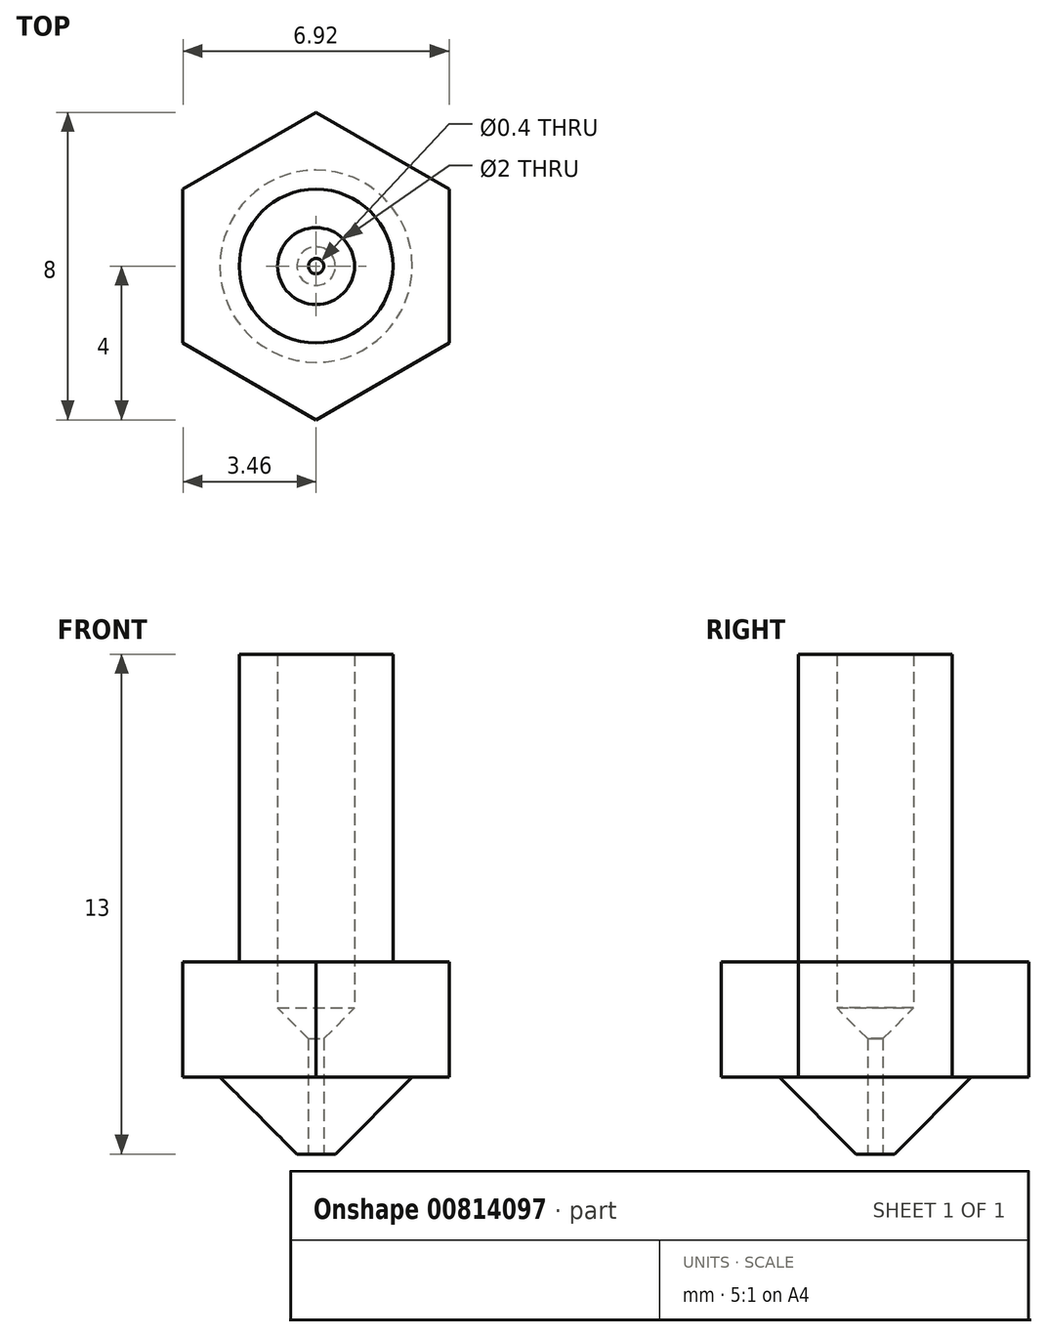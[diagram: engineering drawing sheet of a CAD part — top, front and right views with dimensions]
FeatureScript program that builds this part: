
annotation { "Feature Type Name" : "Feature", "Feature Type Description" : "" }
export const myFeature = defineFeature(function(context is Context, id is Id, definition is map)
    precondition{}
    {
        {
            var Q0;
            Q0=qCreatedBy(makeId("Front.planeOp"),FACE);
            var sketch = newSketch(context, id + "F0", { "sketchPlane" : qUnion([Q0])});
            skLineSegment(sketch, "E0", {"start": v(0, 0) * mm, "end": v(0, 10.14) * mm, "construction": true});
            skLineSegment(sketch, "E1", {"start": v(0.2, 0) * mm, "end": v(0.5, 0) * mm});
            skLineSegment(sketch, "E2", {"start": v(0.5, 0) * mm, "end": v(2.5, 2) * mm});
            skLineSegment(sketch, "E3", {"start": v(2.5, 2) * mm, "end": v(4, 2) * mm});
            skLineSegment(sketch, "E4", {"start": v(4, 2) * mm, "end": v(4, 5) * mm});
            skLineSegment(sketch, "E5", {"start": v(4, 5) * mm, "end": v(2, 5) * mm});
            skLineSegment(sketch, "E6", {"start": v(2, 5) * mm, "end": v(2, 13) * mm});
            skLineSegment(sketch, "E7", {"start": v(2, 13) * mm, "end": v(0.2, 13) * mm});
            skLineSegment(sketch, "E8", {"start": v(0.2, 13) * mm, "end": v(0.2, 0) * mm});
            skLineSegment(sketch, "E9", {"start": v(1, 13) * mm, "end": v(1, 3.8) * mm});
            skLineSegment(sketch, "E10", {"start": v(1, 3.8) * mm, "end": v(0.2, 3) * mm});
            skSolve(sketch);
        }
        {
            var Q0;
            {var subQ0=sQuery(id+"F0.wireOp",EDGE,"E1");Q0=makeQuery(id+"F0.imprint","IMPRINT",FACE,{"disambiguationData":[TD([[makeQuery(id+"F0.imprint","IMPRINT",EDGE,{"derivedFrom":subQ0}),1.0]])]});}
            var Q1;
            Q1=sQuery(id+"F0.wireOp",EDGE,"E0");
            revolve(context, id + "F1", {"surfaceOperationType" : NewSurfaceOperationType.NEW, "entities" : qUnion([Q0]), "axis" : qUnion([Q1]), "revolveType" : RevolveType.FULL});
        }
        {
            var Q0;
            Q0=makeQuery(id+"F1.opRevolve","SWEPT_FACE",FACE,{"disambiguationData":[OSD([sQuery(id+"F0.wireOp",EDGE,"E3")])]});
            var sketch = newSketch(context, id + "F2", { "sketchPlane" : qUnion([Q0])});
            skCircle(sketch, "E11.cCircle", {"center": v(0, 0) * mm, "radius": 3.46 * mm, "construction": true});
            skLineSegment(sketch, "E11.0", {"start": v(3.46, 2) * mm, "end": v(3.46, -2) * mm});
            skLineSegment(sketch, "E11.1", {"start": v(3.46, -2) * mm, "end": v(0, -4) * mm});
            skLineSegment(sketch, "E11.2", {"start": v(0, -4) * mm, "end": v(-3.46, -2) * mm});
            skLineSegment(sketch, "E11.3", {"start": v(-3.46, -2) * mm, "end": v(-3.46, 2) * mm});
            skLineSegment(sketch, "E11.4", {"start": v(-3.46, 2) * mm, "end": v(0, 4) * mm});
            skLineSegment(sketch, "E11.5", {"start": v(0, 4) * mm, "end": v(3.46, 2) * mm});
            skPoint(sketch, "E11.0.midPoint", {"position": v(3.46, 0) * mm});
            skSolve(sketch);
        }
        {
            var Q0;
            {var subQ0=sQuery(id+"F2.wireOp",EDGE,"E11.4");Q0=makeQuery(id+"F2.imprint","IMPRINT",FACE,{"disambiguationData":[TD([[makeQuery(id+"F2.imprint","IMPRINT",EDGE,{"derivedFrom":subQ0}),1.0]])]});}
            var Q1;
            {var subQ0=sQuery(id+"F2.wireOp",EDGE,"E11.5");Q1=makeQuery(id+"F2.imprint","IMPRINT",FACE,{"disambiguationData":[TD([[makeQuery(id+"F2.imprint","IMPRINT",EDGE,{"derivedFrom":subQ0}),1.0]])]});}
            var Q2;
            {var subQ0=sQuery(id+"F2.wireOp",EDGE,"E11.0");Q2=makeQuery(id+"F2.imprint","IMPRINT",FACE,{"disambiguationData":[TD([[makeQuery(id+"F2.imprint","IMPRINT",EDGE,{"derivedFrom":subQ0}),1.0]])]});}
            var Q3;
            {var subQ0=sQuery(id+"F2.wireOp",EDGE,"E11.1");Q3=makeQuery(id+"F2.imprint","IMPRINT",FACE,{"disambiguationData":[TD([[makeQuery(id+"F2.imprint","IMPRINT",EDGE,{"derivedFrom":subQ0}),1.0]])]});}
            var Q4;
            {var subQ0=sQuery(id+"F2.wireOp",EDGE,"E11.2");Q4=makeQuery(id+"F2.imprint","IMPRINT",FACE,{"disambiguationData":[TD([[makeQuery(id+"F2.imprint","IMPRINT",EDGE,{"derivedFrom":subQ0}),1.0]])]});}
            var Q5;
            {var subQ0=sQuery(id+"F2.wireOp",EDGE,"E11.3");Q5=makeQuery(id+"F2.imprint","IMPRINT",FACE,{"disambiguationData":[TD([[makeQuery(id+"F2.imprint","IMPRINT",EDGE,{"derivedFrom":subQ0}),1.0]])]});}
            extrude(context, id + "F3", {"entities" : qUnion([Q0, Q1, Q2, Q3, Q4, Q5]), "operationType" : NewBodyOperationType.REMOVE, "oppositeDirection" : true, "depth" : 25 * mm, "offsetDistance" : 25 * mm});
        }
    });
